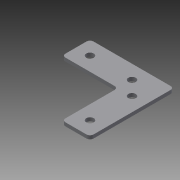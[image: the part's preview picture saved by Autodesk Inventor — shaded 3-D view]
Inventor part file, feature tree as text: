
AUTODESK INVENTOR PART (.ipt)
format: ipt  version: 2013 (Build 170138000, 138)  size: 101,376 bytes
history: native  units: in
note: dims shown in document units (in); Inventor stores cm internally (conversion verified against a paired STEP export)
features: extrude x1, sketch x1
ambient origin geometry x8: Origin, YZ Plane, XZ Plane, XY Plane, X Axis, Y Axis, Z Axis, Center Point
bodies: Solid1 (feature_tree)
feature tree (2):
  extrude  "Extrusion1"  Depth=1.0in
  sketch  "Sketch1"  dims[d0=3.0in d1=1.0in d2=2.0in d3=2.0in d4=1.0in d5=0.266in d6=0.266in d7=0.266in d8=0.266in d9=0.5in d10=0.0in d11=0.5in d12=0.5in d13=0.5in d14=0.5in d15=0.5in d16=0.125in d17=0.125in d18=0.0in]
